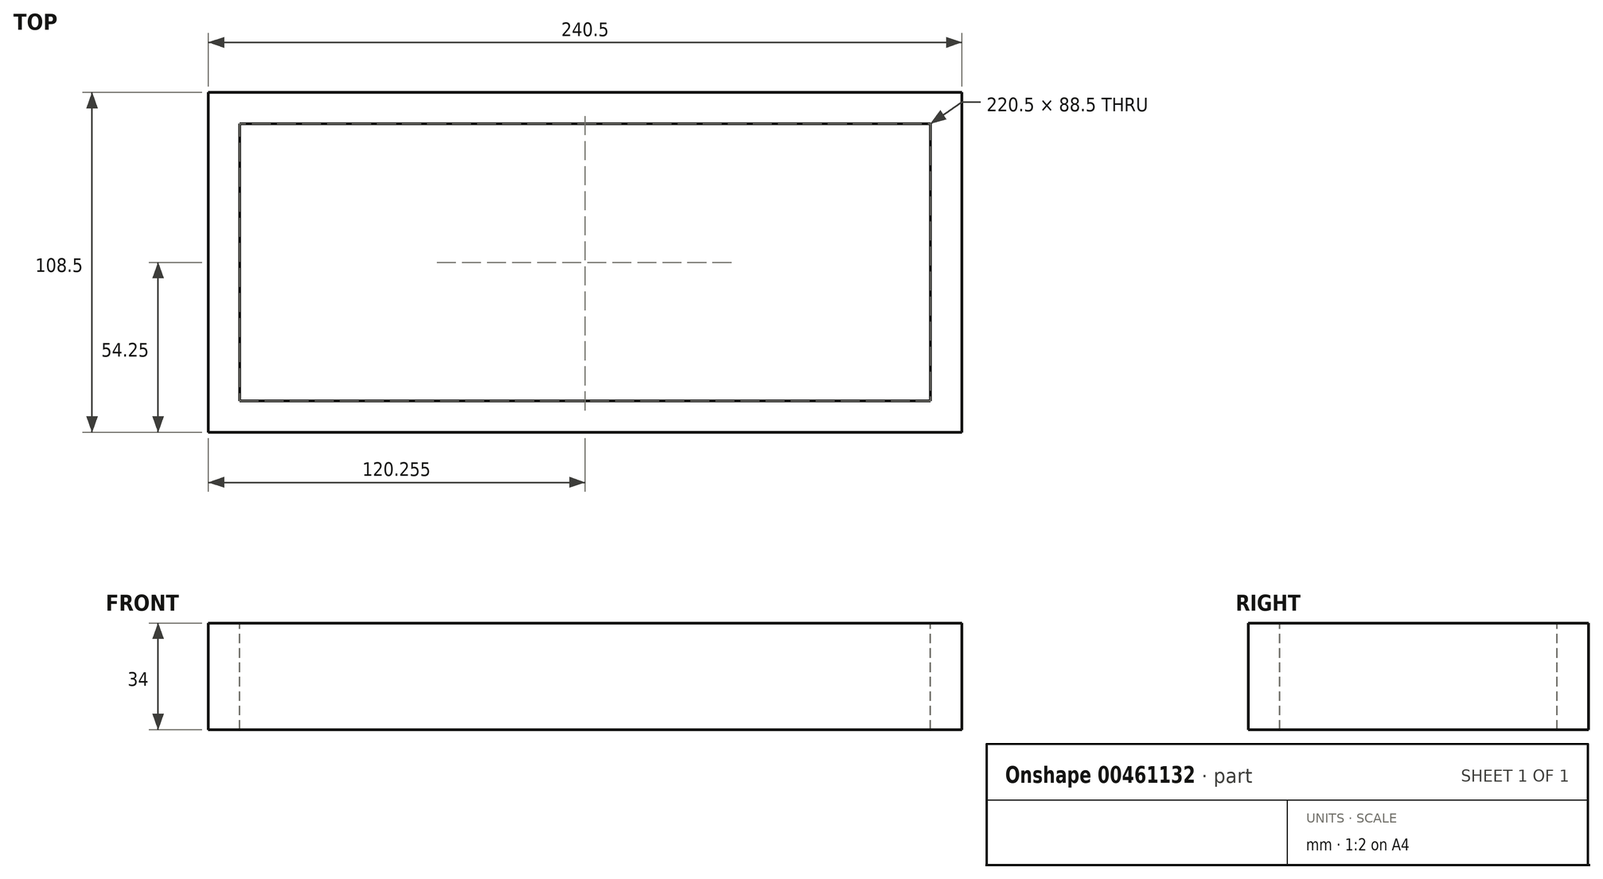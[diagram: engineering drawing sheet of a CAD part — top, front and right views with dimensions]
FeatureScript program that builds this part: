
annotation { "Feature Type Name" : "Feature", "Feature Type Description" : "" }
export const myFeature = defineFeature(function(context is Context, id is Id, definition is map)
    precondition{}
    {
        {
            var Q0;
            Q0=qCreatedBy(makeId("Top.planeOp"),FACE);
            var sketch = newSketch(context, id + "F0", { "sketchPlane" : qUnion([Q0])});
            skLineSegment(sketch, "E0.bottom", {"start": v(-150, 73.27) * mm, "end": v(90.5, 73.27) * mm});
            skLineSegment(sketch, "E0.top", {"start": v(-150, -35.23) * mm, "end": v(90.5, -35.23) * mm});
            skLineSegment(sketch, "E0.left", {"start": v(-150, 73.27) * mm, "end": v(-150, -35.23) * mm});
            skLineSegment(sketch, "E0.right", {"start": v(90.5, 73.27) * mm, "end": v(90.5, -35.23) * mm});
            skSolve(sketch);
        }
        {
            var Q0;
            Q0 = qSketchRegion(id + "F0", true);
            extrude(context, id + "F1", {"entities" : qUnion([Q0]), "depth" : 34 * mm});
        }
        {
            var Q0;
            Q0=makeQuery(id+"F1.opExtrude","CAP_FACE",FACE,{"disambiguationData":[OSD([sQuery(id+"F0.wireOp",EDGE,"E0.bottom"),sQuery(id+"F0.wireOp",EDGE,"E0.top"),sQuery(id+"F0.wireOp",EDGE,"E0.left"),sQuery(id+"F0.wireOp",EDGE,"E0.right")])],"isStart":false});
            var sketch = newSketch(context, id + "F2", { "sketchPlane" : qUnion([Q0])});
            skLineSegment(sketch, "E1", {"start": v(-150, 73.27) * mm, "end": v(90.5, -35.23) * mm, "construction": true});
            skLineSegment(sketch, "E2", {"start": v(-29.75, 19.02) * mm, "end": v(-29.75, 63.27) * mm, "construction": true});
            skLineSegment(sketch, "E3", {"start": v(-29.75, 19.02) * mm, "end": v(-29.75, -25.23) * mm, "construction": true});
            skLineSegment(sketch, "E4", {"start": v(80.5, -25.23) * mm, "end": v(80.5, 63.27) * mm});
            skLineSegment(sketch, "E5", {"start": v(-140, -25.23) * mm, "end": v(-140, 63.27) * mm});
            skLineSegment(sketch, "E6", {"start": v(80.5, -25.23) * mm, "end": v(-140, -25.23) * mm});
            skLineSegment(sketch, "E7", {"start": v(80.5, 63.27) * mm, "end": v(-140, 63.27) * mm});
            skSolve(sketch);
        }
        {
            var Q0;
            Q0 = qSketchRegion(id + "F2", true);
            extrude(context, id + "F3", {"entities" : qUnion([Q0]), "operationType" : NewBodyOperationType.REMOVE, "oppositeDirection" : true, "depth" : 34 * mm});
        }
    });
